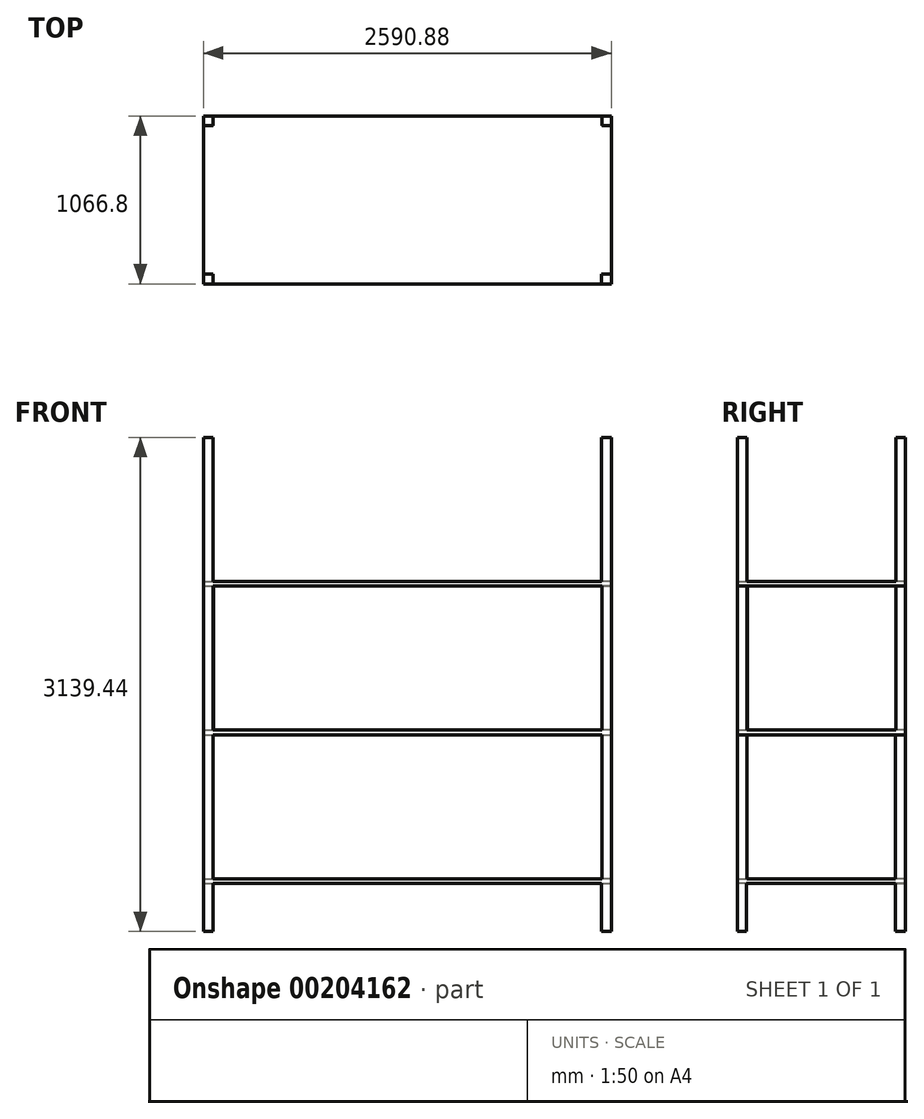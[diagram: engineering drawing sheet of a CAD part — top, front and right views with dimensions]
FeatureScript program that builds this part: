
annotation { "Feature Type Name" : "Feature", "Feature Type Description" : "" }
export const myFeature = defineFeature(function(context is Context, id is Id, definition is map)
    precondition{}
    {
        {
            var Q0;
            Q0=qCreatedBy(makeId("Top.planeOp"),FACE);
            var sketch = newSketch(context, id + "F0", { "sketchPlane" : qUnion([Q0])});
            skLineSegment(sketch, "E0.bottom", {"start": v(0, 0) * mm, "end": v(2590.8, 0) * mm});
            skLineSegment(sketch, "E0.top", {"start": v(0, 1066.8) * mm, "end": v(2590.8, 1066.8) * mm});
            skLineSegment(sketch, "E0.left", {"start": v(0, 0) * mm, "end": v(0, 1066.8) * mm});
            skLineSegment(sketch, "E0.right", {"start": v(2590.8, 0) * mm, "end": v(2590.8, 1066.8) * mm});
            skSolve(sketch);
        }
        {
            var Q0;
            Q0 = qSketchRegion(id + "F0", true);
            extrude(context, id + "F1", {"entities" : qUnion([Q0]), "depth" : 30.48 * mm});
        }
        {
            var Q0;
            Q0=makeQuery(id+"F1.opExtrude","CAP_FACE",FACE,{"disambiguationData":[OSD([sQuery(id+"F0.wireOp",EDGE,"E0.bottom"),sQuery(id+"F0.wireOp",EDGE,"E0.top"),sQuery(id+"F0.wireOp",EDGE,"E0.left"),sQuery(id+"F0.wireOp",EDGE,"E0.right")])],"isStart":false});
            var sketch = newSketch(context, id + "F2", { "sketchPlane" : qUnion([Q0])});
            skLineSegment(sketch, "E1.bottom", {"start": v(0, 1066.8) * mm, "end": v(60.96, 1066.8) * mm});
            skLineSegment(sketch, "E1.top", {"start": v(0, 1005.84) * mm, "end": v(60.96, 1005.84) * mm});
            skLineSegment(sketch, "E1.left", {"start": v(0, 1066.8) * mm, "end": v(0, 1005.84) * mm});
            skLineSegment(sketch, "E1.right", {"start": v(60.96, 1066.8) * mm, "end": v(60.96, 1005.84) * mm});
            skLineSegment(sketch, "E2.bottom", {"start": v(0, 0) * mm, "end": v(60.96, 0) * mm});
            skLineSegment(sketch, "E2.top", {"start": v(0, 60.96) * mm, "end": v(60.96, 60.96) * mm});
            skLineSegment(sketch, "E2.left", {"start": v(0, 0) * mm, "end": v(0, 60.96) * mm});
            skLineSegment(sketch, "E2.right", {"start": v(60.96, 0) * mm, "end": v(60.96, 60.96) * mm});
            skLineSegment(sketch, "E3.bottom", {"start": v(2590.8, 1066.8) * mm, "end": v(2529.84, 1066.8) * mm});
            skLineSegment(sketch, "E3.top", {"start": v(2590.8, 1005.84) * mm, "end": v(2529.84, 1005.84) * mm});
            skLineSegment(sketch, "E3.left", {"start": v(2590.8, 1066.8) * mm, "end": v(2590.8, 1005.84) * mm});
            skLineSegment(sketch, "E3.right", {"start": v(2529.84, 1066.8) * mm, "end": v(2529.84, 1005.84) * mm});
            skLineSegment(sketch, "E4.bottom", {"start": v(2590.8, 0) * mm, "end": v(2529.84, 0) * mm});
            skLineSegment(sketch, "E4.top", {"start": v(2590.8, 60.96) * mm, "end": v(2529.84, 60.96) * mm});
            skLineSegment(sketch, "E4.left", {"start": v(2590.8, 0) * mm, "end": v(2590.8, 60.96) * mm});
            skLineSegment(sketch, "E4.right", {"start": v(2529.84, 0) * mm, "end": v(2529.84, 60.96) * mm});
            skSolve(sketch);
        }
        {
            var Q0;
            Q0=makeQuery(id+"F2.imprint","IMPRINT",FACE,{"disambiguationData":[TD([[makeQuery(id+"F2.imprint","IMPRINT",EDGE,{"derivedFrom":sQuery(id+"F2.wireOp",EDGE,"E1.bottom")}),-1.0]])]});
            var Q1;
            Q1=makeQuery(id+"F2.imprint","IMPRINT",FACE,{"disambiguationData":[TD([[makeQuery(id+"F2.imprint","IMPRINT",EDGE,{"derivedFrom":sQuery(id+"F2.wireOp",EDGE,"E2.bottom")}),1.0]])]});
            var Q2;
            Q2=makeQuery(id+"F2.imprint","IMPRINT",FACE,{"disambiguationData":[TD([[makeQuery(id+"F2.imprint","IMPRINT",EDGE,{"derivedFrom":sQuery(id+"F2.wireOp",EDGE,"E4.bottom")}),1.0]])]});
            var Q3;
            Q3=makeQuery(id+"F2.imprint","IMPRINT",FACE,{"disambiguationData":[TD([[makeQuery(id+"F2.imprint","IMPRINT",EDGE,{"derivedFrom":sQuery(id+"F2.wireOp",EDGE,"E3.bottom")}),-1.0]])]});
            extrude(context, id + "F3", {"entities" : qUnion([Q0, Q1, Q2, Q3]), "operationType" : NewBodyOperationType.ADD, "depth" : 914.4 * mm});
        }
        {
            var Q0;
            Q0=makeQuery(id+"F3.opExtrude","CAP_FACE",FACE,{"disambiguationData":[OSD([sQuery(id+"F2.wireOp",EDGE,"E2.bottom"),sQuery(id+"F2.wireOp",EDGE,"E2.top"),sQuery(id+"F2.wireOp",EDGE,"E2.left"),sQuery(id+"F2.wireOp",EDGE,"E2.right")])],"isStart":false});
            var sketch = newSketch(context, id + "F4", { "sketchPlane" : qUnion([Q0])});
            skLineSegment(sketch, "E5.bottom", {"start": v(0, 0) * mm, "end": v(2590.32, 0) * mm});
            skLineSegment(sketch, "E5.top", {"start": v(0, 1066.14) * mm, "end": v(2590.32, 1066.14) * mm});
            skLineSegment(sketch, "E5.left", {"start": v(0, 0) * mm, "end": v(0, 1066.14) * mm});
            skLineSegment(sketch, "E5.right", {"start": v(2590.32, 0) * mm, "end": v(2590.32, 1066.14) * mm});
            skSolve(sketch);
        }
        {
            var Q0;
            Q0 = qSketchRegion(id + "F4", true);
            extrude(context, id + "F5", {"entities" : qUnion([Q0]), "operationType" : NewBodyOperationType.ADD, "depth" : 30.48 * mm});
        }
        {
            var Q0;
            Q0=makeQuery(id+"F5.opExtrude","CAP_FACE",FACE,{"disambiguationData":[OSD([sQuery(id+"F4.wireOp",EDGE,"E5.bottom"),sQuery(id+"F4.wireOp",EDGE,"E5.top"),sQuery(id+"F4.wireOp",EDGE,"E5.left"),sQuery(id+"F4.wireOp",EDGE,"E5.right")])],"isStart":false});
            var sketch = newSketch(context, id + "F6", { "sketchPlane" : qUnion([Q0])});
            skLineSegment(sketch, "E6.bottom", {"start": v(0, 0) * mm, "end": v(61.62, 0) * mm});
            skLineSegment(sketch, "E6.top", {"start": v(0, 63.27) * mm, "end": v(61.62, 63.27) * mm});
            skLineSegment(sketch, "E6.left", {"start": v(0, 0) * mm, "end": v(0, 63.27) * mm});
            skLineSegment(sketch, "E6.right", {"start": v(61.62, 0) * mm, "end": v(61.62, 63.27) * mm});
            skLineSegment(sketch, "E7.bottom", {"start": v(0, 1066.14) * mm, "end": v(63.47, 1066.14) * mm});
            skLineSegment(sketch, "E7.top", {"start": v(0, 1006.55) * mm, "end": v(63.47, 1006.55) * mm});
            skLineSegment(sketch, "E7.left", {"start": v(0, 1066.14) * mm, "end": v(0, 1006.55) * mm});
            skLineSegment(sketch, "E7.right", {"start": v(63.47, 1066.14) * mm, "end": v(63.47, 1006.55) * mm});
            skLineSegment(sketch, "E8.bottom", {"start": v(2590.32, 1066.14) * mm, "end": v(2531, 1066.14) * mm});
            skLineSegment(sketch, "E8.top", {"start": v(2590.32, 1008.45) * mm, "end": v(2531, 1008.45) * mm});
            skLineSegment(sketch, "E8.left", {"start": v(2590.32, 1066.14) * mm, "end": v(2590.32, 1008.45) * mm});
            skLineSegment(sketch, "E8.right", {"start": v(2531, 1066.14) * mm, "end": v(2531, 1008.45) * mm});
            skLineSegment(sketch, "E9.bottom", {"start": v(2590.32, 0) * mm, "end": v(2531.23, 0) * mm});
            skLineSegment(sketch, "E9.top", {"start": v(2590.32, 60.17) * mm, "end": v(2531.23, 60.17) * mm});
            skLineSegment(sketch, "E9.left", {"start": v(2590.32, 0) * mm, "end": v(2590.32, 60.17) * mm});
            skLineSegment(sketch, "E9.right", {"start": v(2531.23, 0) * mm, "end": v(2531.23, 60.17) * mm});
            skSolve(sketch);
        }
        {
            var Q0;
            Q0 = qSketchRegion(id + "F6", true);
            extrude(context, id + "F7", {"entities" : qUnion([Q0]), "operationType" : NewBodyOperationType.ADD, "depth" : 914.4 * mm});
        }
        {
            var Q0;
            Q0=makeQuery(id+"F7.opExtrude","CAP_FACE",FACE,{"disambiguationData":[OSD([sQuery(id+"F6.wireOp",EDGE,"E6.bottom"),sQuery(id+"F6.wireOp",EDGE,"E6.top"),sQuery(id+"F6.wireOp",EDGE,"E6.left"),sQuery(id+"F6.wireOp",EDGE,"E6.right")])],"isStart":false});
            var sketch = newSketch(context, id + "F8", { "sketchPlane" : qUnion([Q0])});
            skLineSegment(sketch, "E10.bottom", {"start": v(0, 0) * mm, "end": v(2590.88, 0) * mm});
            skLineSegment(sketch, "E10.top", {"start": v(0, 1066.7) * mm, "end": v(2590.88, 1066.7) * mm});
            skLineSegment(sketch, "E10.left", {"start": v(0, 0) * mm, "end": v(0, 1066.7) * mm});
            skLineSegment(sketch, "E10.right", {"start": v(2590.88, 0) * mm, "end": v(2590.88, 1066.7) * mm});
            skSolve(sketch);
        }
        {
            var Q0;
            Q0 = qSketchRegion(id + "F8", true);
            extrude(context, id + "F9", {"entities" : qUnion([Q0]), "operationType" : NewBodyOperationType.ADD, "depth" : 30.48 * mm});
        }
        {
            var Q0;
            Q0=makeQuery(id+"F9.opExtrude","CAP_FACE",FACE,{"disambiguationData":[OSD([sQuery(id+"F8.wireOp",EDGE,"E10.bottom"),sQuery(id+"F8.wireOp",EDGE,"E10.top"),sQuery(id+"F8.wireOp",EDGE,"E10.left"),sQuery(id+"F8.wireOp",EDGE,"E10.right")])],"isStart":false});
            var sketch = newSketch(context, id + "F10", { "sketchPlane" : qUnion([Q0])});
            skLineSegment(sketch, "E11.bottom", {"start": v(0, 1066.7) * mm, "end": v(61.28, 1066.7) * mm});
            skLineSegment(sketch, "E11.top", {"start": v(0, 1006.32) * mm, "end": v(61.28, 1006.32) * mm});
            skLineSegment(sketch, "E11.left", {"start": v(0, 1066.7) * mm, "end": v(0, 1006.32) * mm});
            skLineSegment(sketch, "E11.right", {"start": v(61.28, 1066.7) * mm, "end": v(61.28, 1006.32) * mm});
            skLineSegment(sketch, "E12.bottom", {"start": v(0, 0) * mm, "end": v(61.28, 0) * mm});
            skLineSegment(sketch, "E12.top", {"start": v(0, 61.9) * mm, "end": v(61.28, 61.9) * mm});
            skLineSegment(sketch, "E12.left", {"start": v(0, 0) * mm, "end": v(0, 61.9) * mm});
            skLineSegment(sketch, "E12.right", {"start": v(61.28, 0) * mm, "end": v(61.28, 61.9) * mm});
            skLineSegment(sketch, "E13.bottom", {"start": v(2590.88, 0) * mm, "end": v(2529.15, 0) * mm});
            skLineSegment(sketch, "E13.top", {"start": v(2590.88, 61.68) * mm, "end": v(2529.15, 61.68) * mm});
            skLineSegment(sketch, "E13.left", {"start": v(2590.88, 0) * mm, "end": v(2590.88, 61.68) * mm});
            skLineSegment(sketch, "E13.right", {"start": v(2529.15, 0) * mm, "end": v(2529.15, 61.68) * mm});
            skLineSegment(sketch, "E14.bottom", {"start": v(2590.88, 1066.7) * mm, "end": v(2530.4, 1066.7) * mm});
            skLineSegment(sketch, "E14.top", {"start": v(2590.88, 1006.32) * mm, "end": v(2530.4, 1006.32) * mm});
            skLineSegment(sketch, "E14.left", {"start": v(2590.88, 1066.7) * mm, "end": v(2590.88, 1006.32) * mm});
            skLineSegment(sketch, "E14.right", {"start": v(2530.4, 1066.7) * mm, "end": v(2530.4, 1006.32) * mm});
            skSolve(sketch);
        }
        {
            var Q0;
            Q0 = qSketchRegion(id + "F10", true);
            extrude(context, id + "F11", {"entities" : qUnion([Q0]), "operationType" : NewBodyOperationType.ADD, "depth" : 914.4 * mm});
        }
        {
            var Q0;
            Q0=makeQuery(id+"F1.opExtrude","CAP_FACE",FACE,{"disambiguationData":[OSD([sQuery(id+"F0.wireOp",EDGE,"E0.bottom"),sQuery(id+"F0.wireOp",EDGE,"E0.top"),sQuery(id+"F0.wireOp",EDGE,"E0.left"),sQuery(id+"F0.wireOp",EDGE,"E0.right")])],"isStart":true});
            var sketch = newSketch(context, id + "F12", { "sketchPlane" : qUnion([Q0])});
            skLineSegment(sketch, "E15.bottom", {"start": v(0, 0) * mm, "end": v(61.63, 0) * mm});
            skLineSegment(sketch, "E15.top", {"start": v(0, -59.57) * mm, "end": v(61.63, -59.57) * mm});
            skLineSegment(sketch, "E15.left", {"start": v(0, 0) * mm, "end": v(0, -59.57) * mm});
            skLineSegment(sketch, "E15.right", {"start": v(61.63, 0) * mm, "end": v(61.63, -59.57) * mm});
            skLineSegment(sketch, "E16.bottom", {"start": v(0, -1066.8) * mm, "end": v(61.63, -1066.8) * mm});
            skLineSegment(sketch, "E16.top", {"start": v(0, -1006.56) * mm, "end": v(61.63, -1006.56) * mm});
            skLineSegment(sketch, "E16.left", {"start": v(0, -1066.8) * mm, "end": v(0, -1006.56) * mm});
            skLineSegment(sketch, "E16.right", {"start": v(61.63, -1066.8) * mm, "end": v(61.63, -1006.56) * mm});
            skLineSegment(sketch, "E17.bottom", {"start": v(2529.23, -59.57) * mm, "end": v(2590.8, -59.57) * mm});
            skLineSegment(sketch, "E17.top", {"start": v(2529.23, 0) * mm, "end": v(2590.8, 0) * mm});
            skLineSegment(sketch, "E17.left", {"start": v(2529.23, -59.57) * mm, "end": v(2529.23, 0) * mm});
            skLineSegment(sketch, "E17.right", {"start": v(2590.8, -59.57) * mm, "end": v(2590.8, 0) * mm});
            skLineSegment(sketch, "E18.bottom", {"start": v(2528.91, -1005.62) * mm, "end": v(2590.8, -1005.62) * mm});
            skLineSegment(sketch, "E18.top", {"start": v(2528.91, -1066.8) * mm, "end": v(2590.8, -1066.8) * mm});
            skLineSegment(sketch, "E18.left", {"start": v(2528.91, -1005.62) * mm, "end": v(2528.91, -1066.8) * mm});
            skLineSegment(sketch, "E18.right", {"start": v(2590.8, -1005.62) * mm, "end": v(2590.8, -1066.8) * mm});
            skSolve(sketch);
        }
        {
            var Q0;
            Q0 = qSketchRegion(id + "F12", true);
            extrude(context, id + "F13", {"entities" : qUnion([Q0]), "operationType" : NewBodyOperationType.ADD, "depth" : 304.8 * mm});
        }
    });
